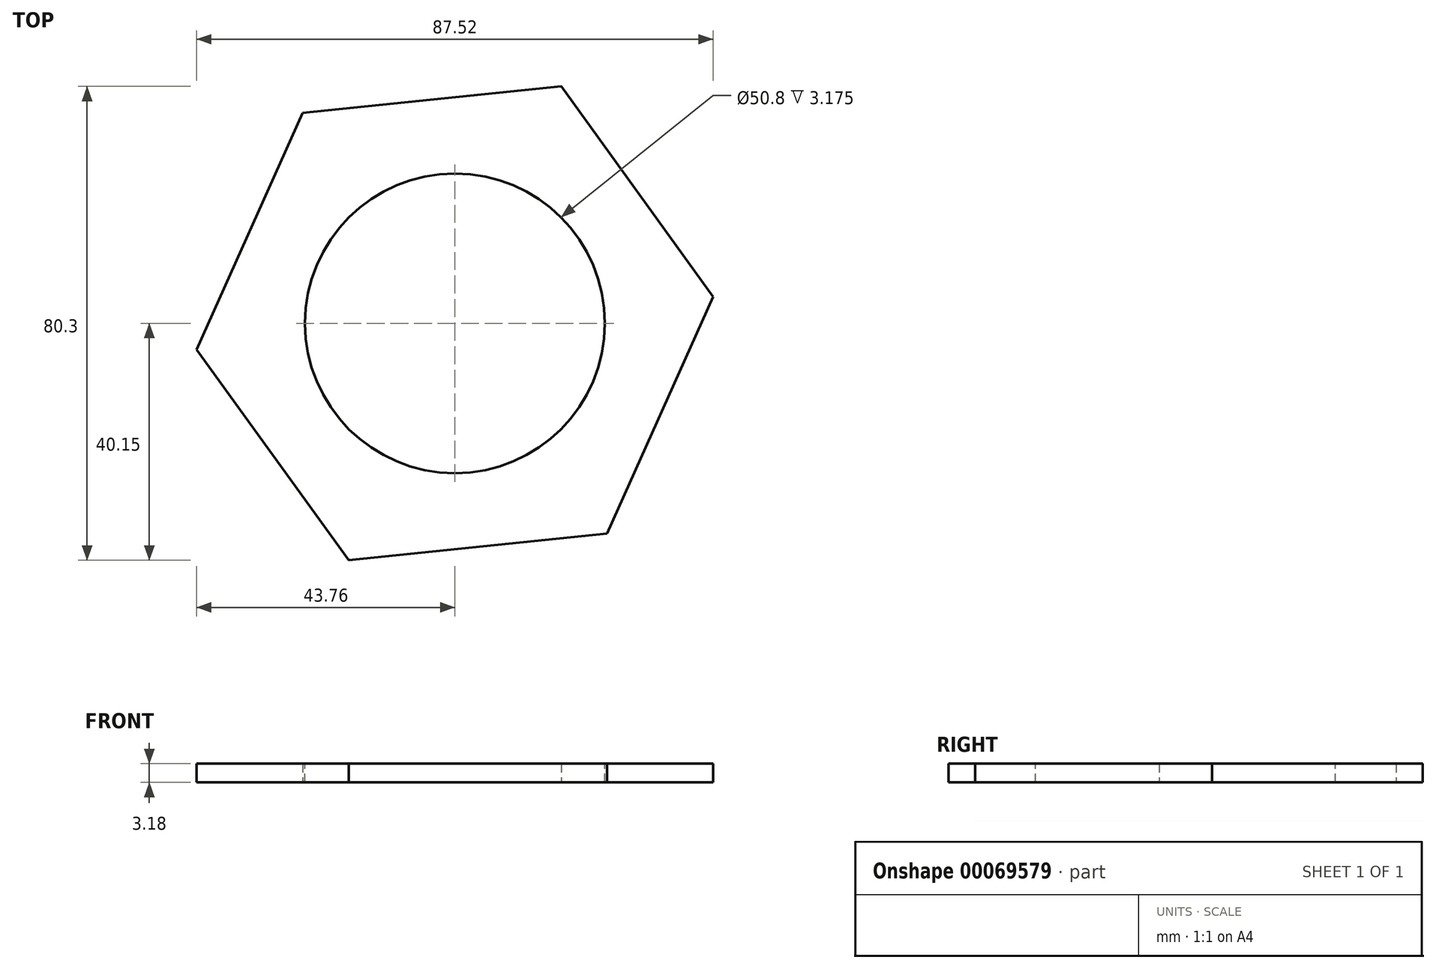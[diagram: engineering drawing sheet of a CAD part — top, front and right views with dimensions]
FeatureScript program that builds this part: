
annotation { "Feature Type Name" : "Feature", "Feature Type Description" : "" }
export const myFeature = defineFeature(function(context is Context, id is Id, definition is map)
    precondition{}
    {
        {
            var Q0;
            Q0=qCreatedBy(makeId("Top.planeOp"),FACE);
            var sketch = newSketch(context, id + "F0", { "sketchPlane" : qUnion([Q0])});
            skCircle(sketch, "E0.cCircle", {"center": v(0, 0) * mm, "radius": 38.1 * mm, "construction": true});
            skLineSegment(sketch, "E0.0", {"start": v(-25.77, 35.66) * mm, "end": v(18, 40.15) * mm});
            skLineSegment(sketch, "E0.1", {"start": v(18, 40.15) * mm, "end": v(43.76, 4.5) * mm});
            skLineSegment(sketch, "E0.2", {"start": v(43.76, 4.5) * mm, "end": v(25.77, -35.66) * mm});
            skLineSegment(sketch, "E0.3", {"start": v(25.77, -35.66) * mm, "end": v(-18, -40.15) * mm});
            skLineSegment(sketch, "E0.4", {"start": v(-18, -40.15) * mm, "end": v(-43.76, -4.5) * mm});
            skLineSegment(sketch, "E0.5", {"start": v(-43.76, -4.5) * mm, "end": v(-25.77, 35.66) * mm});
            skPoint(sketch, "E0.0.midPoint", {"position": v(-3.89, 37.9) * mm});
            skSolve(sketch);
        }
        {
            var Q0;
            Q0=makeQuery(id+"F0.imprint","IMPRINT",FACE,{"disambiguationData":[TD([[makeQuery(id+"F0.imprint","IMPRINT",EDGE,{"derivedFrom":sQuery(id+"F0.wireOp",EDGE,"E0.0")}),-1.0]])]});
            extrude(context, id + "F1", {"entities" : qUnion([Q0]), "depth" : 3.17 * mm});
        }
        {
            var Q0;
            Q0=makeQuery(id+"F1.opExtrude","CAP_FACE",FACE,{"disambiguationData":[OSD([sQuery(id+"F0.wireOp",EDGE,"E0.0"),sQuery(id+"F0.wireOp",EDGE,"E0.1"),sQuery(id+"F0.wireOp",EDGE,"E0.2"),sQuery(id+"F0.wireOp",EDGE,"E0.3"),sQuery(id+"F0.wireOp",EDGE,"E0.4"),sQuery(id+"F0.wireOp",EDGE,"E0.5")])],"isStart":false});
            var sketch = newSketch(context, id + "F2", { "sketchPlane" : qUnion([Q0])});
            skCircle(sketch, "E1", {"center": v(0, 0) * mm, "radius": 25.4 * mm});
            skSolve(sketch);
        }
        {
            var Q0;
            Q0 = qSketchRegion(id + "F2", true);
            extrude(context, id + "F3", {"entities" : qUnion([Q0]), "operationType" : NewBodyOperationType.REMOVE, "oppositeDirection" : true, "depth" : 25.4 * mm});
        }
    });
